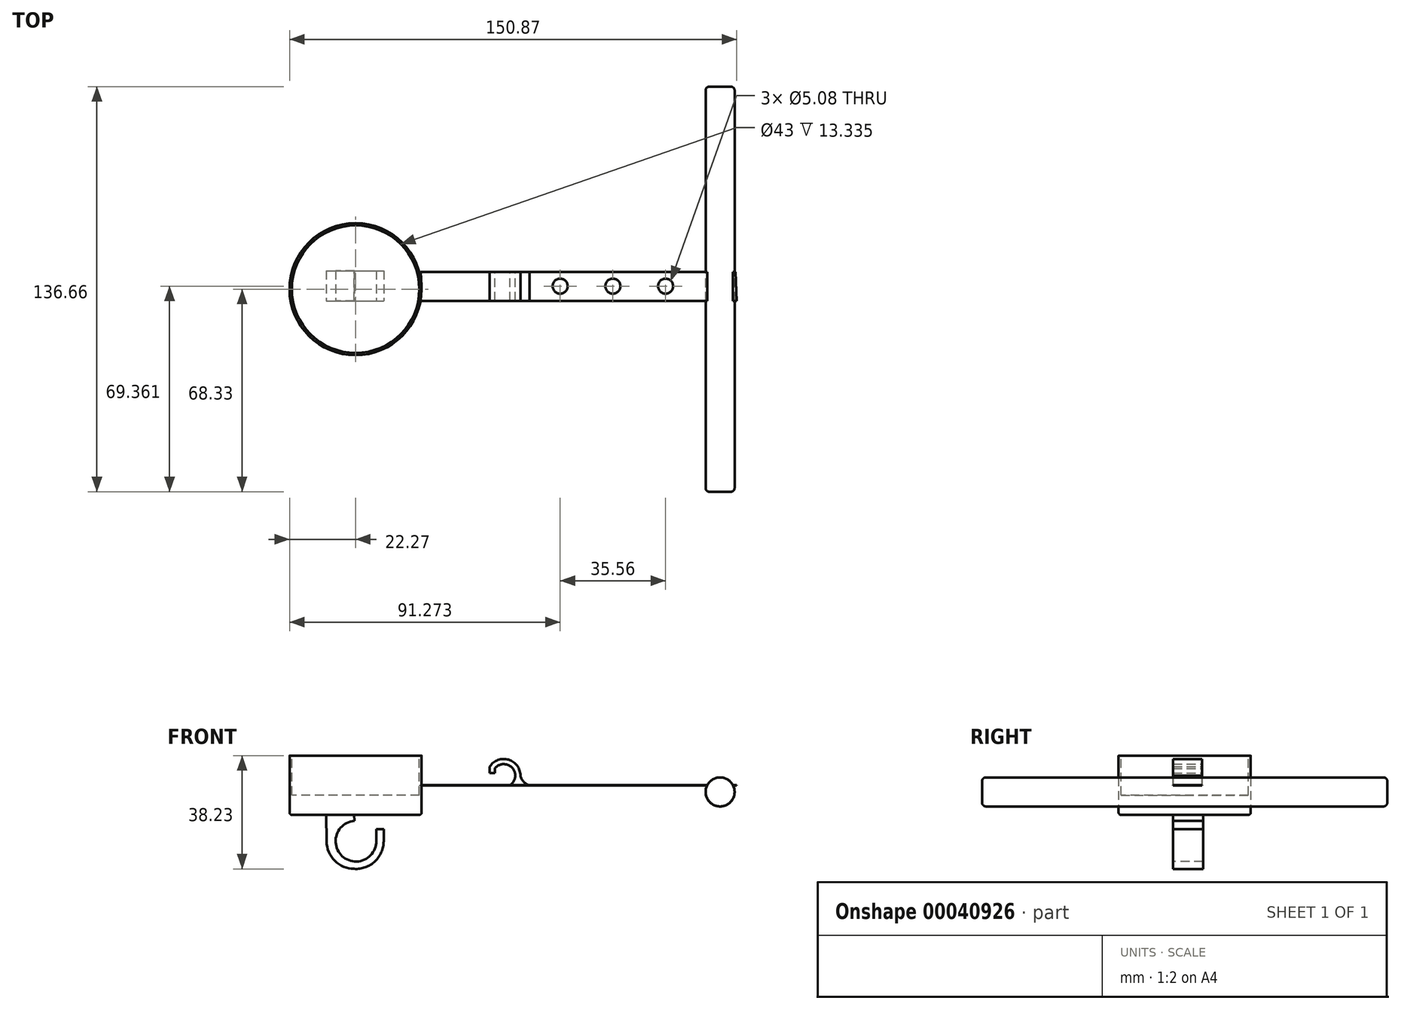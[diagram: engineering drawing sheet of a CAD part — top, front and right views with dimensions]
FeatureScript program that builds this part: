
annotation { "Feature Type Name" : "Feature", "Feature Type Description" : "" }
export const myFeature = defineFeature(function(context is Context, id is Id, definition is map)
    precondition{}
    {
        {
            var Q0;
            Q0=qCreatedBy(makeId("Top.planeOp"),FACE);
            var sketch = newSketch(context, id + "F0", { "sketchPlane" : qUnion([Q0])});
            skLineSegment(sketch, "E0.left", {"start": v(-51.13, 5.84) * mm, "end": v(-50.64, -3.94) * mm});
            skLineSegment(sketch, "E0.right", {"start": v(54.97, 5.84) * mm, "end": v(55.46, -3.94) * mm});
            skCircle(sketch, "E1", {"center": v(-73.14, 0) * mm, "radius": 22.27 * mm});
            skLineSegment(sketch, "E2", {"start": v(55.46, -3.94) * mm, "end": v(-50.64, -3.94) * mm});
            skLineSegment(sketch, "E3", {"start": v(-51.13, 5.84) * mm, "end": v(54.97, 5.84) * mm});
            skLineSegment(sketch, "E4", {"start": v(-50.64, -3.94) * mm, "end": v(-51.22, -3.94) * mm});
            skLineSegment(sketch, "E5", {"start": v(-51.13, 5.84) * mm, "end": v(-51.64, 5.81) * mm});
            skLineSegment(sketch, "E6", {"start": v(51.06, -3.94) * mm, "end": v(32.05, -3.94) * mm});
            skSolve(sketch);
        }
        {
            var Q0;
            {var subQ3=sQuery(id+"F0.wireOp",EDGE,"E0.bottom");var subQ5=sQuery(id+"F0.wireOp",EDGE,"E0.left");var subQ6=makeQuery(id+"F0.imprint","INTERSECT",VERTEX,{"derivedFrom":[subQ3,subQ5]});Q0=makeQuery(id+"F0.imprint","IMPRINT",FACE,{"disambiguationData":[TD([[makeQuery(id+"F0.imprint","IMPRINT",EDGE,{"disambiguationData":[TD([[subQ6,-1.0]])],"derivedFrom":subQ3}),-1.0]])]});}
            var Q1;
            {var subQ5=sQuery(id+"F0.wireOp",EDGE,"E0.right");Q1=makeQuery(id+"F0.imprint","IMPRINT",FACE,{"disambiguationData":[TD([[makeQuery(id+"F0.imprint","IMPRINT",EDGE,{"derivedFrom":subQ5}),-1.0]])]});}
            var Q2;
            {var subQ3=sQuery(id+"F0.wireOp",EDGE,"E2");Q2=makeQuery(id+"F0.imprint","IMPRINT",FACE,{"disambiguationData":[TD([[makeQuery(id+"F0.imprint","IMPRINT",EDGE,{"derivedFrom":subQ3}),-1.0]])]});}
            var Q3;
            {var subQ0=sQuery(id+"F0.wireOp",EDGE,"E4");Q3=makeQuery(id+"F0.imprint","IMPRINT",FACE,{"disambiguationData":[TD([[makeQuery(id+"F0.imprint","IMPRINT",EDGE,{"derivedFrom":subQ0}),-1.0]])]});}
            extrude(context, id + "F1", {"entities" : qUnion([Q0, Q1, Q2, Q3]), "oppositeDirection" : true, "depth" : 1 / 20 * mm});
        }
        {
            var Q0;
            Q0=makeQuery(id+"F0.imprint","IMPRINT",FACE,{"disambiguationData":[TD([[makeQuery(id+"F0.imprint","IMPRINT",EDGE,{"derivedFrom":sQuery(id+"F0.wireOp",EDGE,"E1")}),1.0]])]});
            extrude(context, id + "F2", {"entities" : qUnion([Q0]), "operationType" : NewBodyOperationType.ADD, "endBound" : BoundingType.SYMMETRIC, "depth" : 20 * mm});
        }
        {
            var Q0;
            Q0=makeQuery(id+"F2.opExtrude","CAP_FACE",FACE,{"disambiguationData":[OSD([sQuery(id+"F0.wireOp",EDGE,"E1")])],"isStart":false});
            var sketch = newSketch(context, id + "F3", { "sketchPlane" : qUnion([Q0])});
            skCircle(sketch, "E7", {"center": v(-73.14, 0) * mm, "radius": 21.5 * mm});
            skSolve(sketch);
        }
        {
            var Q0;
            Q0=makeQuery(id+"F2.opExtrude","CAP_EDGE",EDGE,{"disambiguationData":[OSD([sQuery(id+"F0.wireOp",EDGE,"E1")])],"isStart":false});
            fillet(context, id + "F4", {"entities" : qUnion([Q0]), "radius" : .1 * mm, "tangentPropagation" : true, "allowEdgeOverflow" : false});
        }
        {
            var Q0;
            Q0=makeQuery(id+"F2.opExtrude","CAP_FACE",FACE,{"disambiguationData":[OSD([sQuery(id+"F0.wireOp",EDGE,"E1")])],"isStart":true});
            var Q1;
            {var subQ0=sQuery(id+"F0.wireOp",EDGE,"E1");Q1=makeQuery(id+"F4.opFillet","BLEND_EDGE",EDGE,{"blendedFrom":[makeQuery(id+"F2.opExtrude","CAP_EDGE",EDGE,{"disambiguationData":[OSD([subQ0])],"isStart":false}),makeQuery(id+"F2.opExtrude","SWEPT_FACE",FACE,{"disambiguationData":[OSD([subQ0])]})],"blendedInto":[makeQuery(id+"F2.opExtrude","SWEPT_FACE",FACE,{"disambiguationData":[OSD([subQ0])]})]});}
            fillet(context, id + "F5", {"entities" : qUnion([Q0, Q1]), "radius" : .8 * mm, "tangentPropagation" : true, "allowEdgeOverflow" : false});
        }
        {
            var Q0;
            Q0=qCreatedBy(makeId("Front.planeOp"),FACE);
            var sketch = newSketch(context, id + "F6", { "sketchPlane" : qUnion([Q0])});
            skCircle(sketch, "E8", {"center": v(49.81, -2.26) * mm, "radius": 4.89 * mm});
            skSolve(sketch);
        }
        {
            var Q0;
            Q0=makeQuery(id+"F6.imprint","IMPRINT",FACE,{"disambiguationData":[TD([[makeQuery(id+"F6.imprint","IMPRINT",EDGE,{"derivedFrom":sQuery(id+"F6.wireOp",EDGE,"E8")}),1.0]])]});
            extrude(context, id + "F7", {"entities" : qUnion([Q0]), "operationType" : NewBodyOperationType.ADD, "endBound" : BoundingType.SYMMETRIC, "depth" : 136.65 * mm});
        }
        {
            var Q0;
            Q0=makeQuery(id+"F3.imprint","IMPRINT",FACE,{"disambiguationData":[TD([[makeQuery(id+"F3.imprint","IMPRINT",EDGE,{"derivedFrom":sQuery(id+"F3.wireOp",EDGE,"E7")}),1.0]])]});
            var Q1;
            Q1=sQuery(id+"F3.wireOp",EDGE,"E7");
            extrude(context, id + "F8", {"entities" : qUnion([Q0]), "operationType" : NewBodyOperationType.REMOVE, "surfaceEntities" : qUnion([Q1]), "oppositeDirection" : true, "depth" : 13.33 * mm});
        }
        {
            var Q0;
            {var subQ0=sQuery(id+"F0.wireOp",EDGE,"E2");var subQ1=sQuery(id+"F0.wireOp",EDGE,"E4");var subQ2=sQuery(id+"F0.wireOp",EDGE,"E1");Q0=makeQuery(id+"F7.boolean.opBoolean","SPLIT",FACE,{"disambiguationData":[TD([makeQuery(id+"F2.opExtrude","SWEPT_FACE",FACE,{"disambiguationData":[OSD([subQ2])]})])],"derivedFrom":makeQuery(id+"F1.opExtrude","SWEPT_FACE",FACE,{"disambiguationData":[OSD([subQ0,subQ1])]})});}
            var sketch = newSketch(context, id + "F9", { "sketchPlane" : qUnion([Q0])});
            skArc(sketch, "E9", {"start": v(-73.6, -9.51) * mm, "mid": v(-82.92, -18.86) * mm, "end": v(-73.6, -28.2) * mm});
            skLineSegment(sketch, "E10", {"start": v(-73.6, -9.51) * mm, "end": v(-73.6, -6.4) * mm});
            skLineSegment(sketch, "E11", {"start": v(-73.6, -6.4) * mm, "end": v(-83.14, -6.4) * mm});
            skLineSegment(sketch, "E12", {"start": v(-83.14, -6.4) * mm, "end": v(-82.92, -18.98) * mm});
            skArc(sketch, "E13", {"start": v(-73.6, -28.2) * mm, "mid": v(-66.6, -25.69) * mm, "end": v(-63.66, -18.86) * mm});
            skArc(sketch, "E14", {"start": v(-73.53, -12.04) * mm, "mid": v(-77.66, -23.92) * mm, "end": v(-66.15, -18.84) * mm});
            skLineSegment(sketch, "E15", {"start": v(-73.53, -12.04) * mm, "end": v(-73.6, -9.51) * mm});
            skLineSegment(sketch, "E16", {"start": v(-66.15, -18.84) * mm, "end": v(-63.66, -18.86) * mm});
            skLineSegment(sketch, "E17", {"start": v(-95.37, 9.85) * mm, "end": v(-113.67, 9.85) * mm});
            skLineSegment(sketch, "E18", {"start": v(-66.15, -18.84) * mm, "end": v(-66.18, -14.78) * mm});
            skLineSegment(sketch, "E19", {"start": v(-66.18, -14.78) * mm, "end": v(-63.66, -14.76) * mm});
            skLineSegment(sketch, "E20", {"start": v(-63.66, -14.76) * mm, "end": v(-63.66, -18.86) * mm});
            skSolve(sketch);
        }
        {
            var Q0;
            Q0 = qSketchRegion(id + "F9", true);
            extrude(context, id + "F10", {"entities" : qUnion([Q0]), "operationType" : NewBodyOperationType.ADD, "oppositeDirection" : true, "depth" : 10.16 * mm});
        }
        {
            var Q0;
            Q0=makeQuery(id+"F7.opExtrude","CAP_EDGE",EDGE,{"disambiguationData":[OSD([sQuery(id+"F6.wireOp",EDGE,"E8")])],"isStart":true});
            var Q1;
            Q1=makeQuery(id+"F7.opExtrude","CAP_EDGE",EDGE,{"disambiguationData":[OSD([sQuery(id+"F6.wireOp",EDGE,"E8")])],"isStart":false});
            fillet(context, id + "F11", {"entities" : qUnion([Q0, Q1]), "radius" : 1.27 * mm, "tangentPropagation" : true, "allowEdgeOverflow" : false});
        }
        {
            var Q0;
            {var subQ0=sQuery(id+"F0.wireOp",EDGE,"E3");var subQ1=sQuery(id+"F0.wireOp",EDGE,"E0.left");var subQ2=sQuery(id+"F0.wireOp",EDGE,"E0.right");var subQ3=sQuery(id+"F0.wireOp",EDGE,"E1");var subQ4=sQuery(id+"F0.wireOp",EDGE,"E2");var subQ5=sQuery(id+"F0.wireOp",EDGE,"E4");Q0=makeQuery(id+"F7.boolean.opBoolean","SPLIT",FACE,{"disambiguationData":[TD([makeQuery(id+"F1.opExtrude","SWEPT_FACE",FACE,{"disambiguationData":[OSD([subQ1])]}),makeQuery(id+"F1.opExtrude","CAP_FACE",FACE,{"disambiguationData":[OSD([subQ1,subQ2,subQ3,subQ4,subQ0,subQ5])],"isStart":true}),makeQuery(id+"F1.opExtrude","CAP_FACE",FACE,{"disambiguationData":[OSD([subQ1,subQ2,subQ3,subQ4,subQ0,subQ5])],"isStart":false}),makeQuery(id+"F7.opExtrude","SWEPT_FACE",FACE,{"disambiguationData":[OSD([sQuery(id+"F6.wireOp",EDGE,"E8")])]})])],"derivedFrom":makeQuery(id+"F1.opExtrude","SWEPT_FACE",FACE,{"disambiguationData":[OSD([subQ0])]})});}
            var sketch = newSketch(context, id + "F12", { "sketchPlane" : qUnion([Q0])});
            skArc(sketch, "E21", {"start": v(27.86, 6.3) * mm, "mid": v(20, 7.89) * mm, "end": v(18.56, 0) * mm});
            skArc(sketch, "E22", {"start": v(26.16, 5.67) * mm, "mid": v(20.28, 5.83) * mm, "end": v(21.04, 0) * mm});
            skLineSegment(sketch, "E23", {"start": v(27.86, 6.3) * mm, "end": v(27.86, 4.06) * mm});
            skLineSegment(sketch, "E24", {"start": v(26.16, 5.67) * mm, "end": v(26.16, 4.06) * mm});
            skLineSegment(sketch, "E25", {"start": v(26.16, 4.06) * mm, "end": v(27.86, 4.06) * mm});
            skLineSegment(sketch, "E26", {"start": v(18.56, 0) * mm, "end": v(21.04, 0) * mm});
            skArc(sketch, "E27", {"start": v(14.52, 0) * mm, "mid": v(16.46, 1.2) * mm, "end": v(17.53, 3.2) * mm});
            skSolve(sketch);
        }
        {
            var Q0;
            Q0 = qSketchRegion(id + "F12", true);
            var Q1;
            {var subQ5=sQuery(id+"F12.wireOp",EDGE,"E27");Q1=makeQuery(id+"F12.imprint","IMPRINT",FACE,{"disambiguationData":[TD([[makeQuery(id+"F12.imprint","IMPRINT",EDGE,{"derivedFrom":subQ5}),-1.0]])]});}
            extrude(context, id + "F13", {"entities" : qUnion([Q0, Q1]), "operationType" : NewBodyOperationType.ADD, "oppositeDirection" : true, "depth" : 9.76 * mm});
        }
        {
            var Q0;
            {var subQ6=sQuery(id+"F0.wireOp",EDGE,"E0.right");Q0=makeQuery(id+"F0.imprint","IMPRINT",FACE,{"disambiguationData":[TD([[makeQuery(id+"F0.imprint","IMPRINT",EDGE,{"derivedFrom":subQ6}),-1.0]])]});}
            var sketch = newSketch(context, id + "F14", { "sketchPlane" : qUnion([Q0])});
            skCircle(sketch, "E28", {"center": v(13.64, 1.03) * mm, "radius": 2.54 * mm});
            skCircle(sketch, "E29", {"center": v(-4.14, 1.03) * mm, "radius": 2.54 * mm});
            skCircle(sketch, "E30", {"center": v(31.42, 1.03) * mm, "radius": 2.54 * mm});
            skSolve(sketch);
        }
        {
            var Q0;
            Q0 = qSketchRegion(id + "F14", true);
            extrude(context, id + "F15", {"entities" : qUnion([Q0]), "operationType" : NewBodyOperationType.REMOVE, "oppositeDirection" : true, "depth" : 25.4 * mm});
        }
    });
